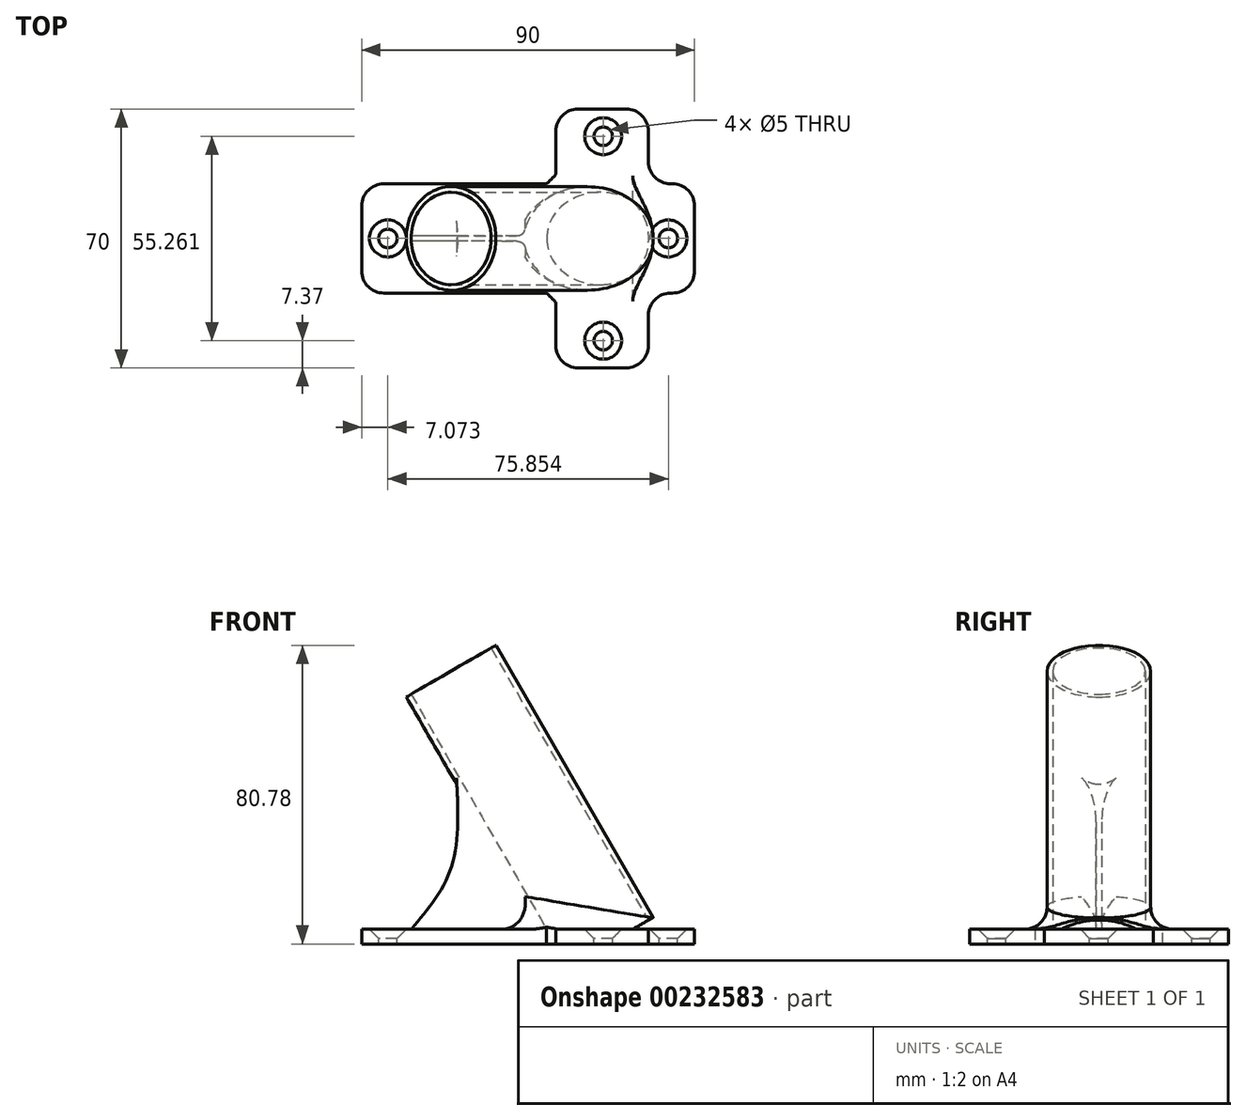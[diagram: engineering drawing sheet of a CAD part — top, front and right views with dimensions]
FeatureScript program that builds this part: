
annotation { "Feature Type Name" : "Feature", "Feature Type Description" : "" }
export const myFeature = defineFeature(function(context is Context, id is Id, definition is map)
    precondition{}
    {
        {
            var Q0;
            Q0=qCreatedBy(makeId("Top.planeOp"),FACE);
            var sketch = newSketch(context, id + "F0", { "sketchPlane" : qUnion([Q0])});
            skLineSegment(sketch, "E0.bottom", {"start": v(45, 14.77) * mm, "end": v(32.5, 14.77) * mm});
            skLineSegment(sketch, "E0.top", {"start": v(45, -14.77) * mm, "end": v(32.5, -14.77) * mm});
            skLineSegment(sketch, "E0.left", {"start": v(45, 14.77) * mm, "end": v(45, -14.77) * mm});
            skLineSegment(sketch, "E0.right", {"start": v(-45, 14.77) * mm, "end": v(-45, -14.77) * mm});
            skPoint(sketch, "E0.middle", {"position": v(0, 0) * mm});
            skCircle(sketch, "E1", {"center": v(37.93, 0) * mm, "radius": 2.5 * mm});
            skCircle(sketch, "E2.MirrorC", {"center": v(-37.93, 0) * mm, "radius": 2.5 * mm});
            skLineSegment(sketch, "E3", {"start": v(-37.93, 0) * mm, "end": v(37.93, 0) * mm, "construction": true});
            skLineSegment(sketch, "E4.bottom", {"start": v(32.5, 35) * mm, "end": v(7.5, 35) * mm});
            skLineSegment(sketch, "E4.top", {"start": v(32.5, -35) * mm, "end": v(7.5, -35) * mm});
            skLineSegment(sketch, "E4.left", {"start": v(32.5, 35) * mm, "end": v(32.5, 14.77) * mm});
            skLineSegment(sketch, "E4.right", {"start": v(7.5, 35) * mm, "end": v(7.5, 14.77) * mm});
            skPoint(sketch, "E4.middle", {"position": v(20, 0) * mm});
            skLineSegment(sketch, "E5.trimOffspring", {"start": v(7.5, -14.77) * mm, "end": v(-45, -14.77) * mm});
            skLineSegment(sketch, "E6.trimOffspring", {"start": v(7.5, 14.77) * mm, "end": v(-45, 14.77) * mm});
            skLineSegment(sketch, "E7.trimOffspring", {"start": v(7.5, -14.77) * mm, "end": v(7.5, -35) * mm});
            skLineSegment(sketch, "E8.trimOffspring", {"start": v(32.5, -14.77) * mm, "end": v(32.5, -35) * mm});
            skCircle(sketch, "E9", {"center": v(20.3, -27.63) * mm, "radius": 2.5 * mm});
            skCircle(sketch, "E10.MirrorC", {"center": v(20.3, 27.63) * mm, "radius": 2.5 * mm});
            skSolve(sketch);
        }
        {
            var Q0;
            Q0=qCreatedBy(makeId("Front.planeOp"),FACE);
            var sketch = newSketch(context, id + "F1", { "sketchPlane" : qUnion([Q0])});
            skLineSegment(sketch, "E11", {"start": v(19.46, 0) * mm, "end": v(14.34, 8.88) * mm, "construction": true});
            skLineSegment(sketch, "E12", {"start": v(-10, 76.03) * mm, "end": v(30, 6.75) * mm});
            skLineSegment(sketch, "E13", {"start": v(30, 6.75) * mm, "end": v(31.3, 7.5) * mm});
            skLineSegment(sketch, "E14", {"start": v(31.3, 7.5) * mm, "end": v(-8.7, 76.78) * mm});
            skLineSegment(sketch, "E15", {"start": v(-8.7, 76.78) * mm, "end": v(-10, 76.03) * mm});
            skSolve(sketch);
        }
        {
            var Q0;
            Q0=makeQuery(id+"F1.imprint","IMPRINT",FACE,{"disambiguationData":[TD([[makeQuery(id+"F1.imprint","IMPRINT",EDGE,{"derivedFrom":sQuery(id+"F1.wireOp",EDGE,"E12")}),1.0]])]});
            var Q1;
            Q1=sQuery(id+"F1.wireOp",EDGE,"E11");
            revolve(context, id + "F2", {"entities" : qUnion([Q0]), "axis" : qUnion([Q1]), "revolveType" : RevolveType.FULL});
        }
        {
            var Q0;
            Q0=makeQuery(id+"F0.imprint","IMPRINT",FACE,{"disambiguationData":[TD([[makeQuery(id+"F0.imprint","IMPRINT",EDGE,{"derivedFrom":sQuery(id+"F0.wireOp",EDGE,"k1UX8Zoy-U4vW-ooh1-YawX-v9qnedj7sq2Y.bottom")}),1.0]])]});
            var Q1;
            Q1=makeQuery(id+"F0.imprint","IMPRINT",FACE,{"disambiguationData":[TD([[makeQuery(id+"F0.imprint","IMPRINT",EDGE,{"derivedFrom":sQuery(id+"F0.wireOp",EDGE,"E0.bottom")}),1.0]])]});
            extrude(context, id + "F3", {"entities" : qUnion([Q0, Q1]), "operationType" : NewBodyOperationType.ADD, "oppositeDirection" : true, "depth" : 4 * mm});
        }
        {
            var Q0;
            Q0=qCreatedBy(makeId("Front.planeOp"),FACE);
            var sketch = newSketch(context, id + "F4", { "sketchPlane" : qUnion([Q0])});
            skLineSegment(sketch, "E16", {"start": v(-19.4, 40.97) * mm, "end": v(4.39, 0) * mm});
            skLineSegment(sketch, "E17", {"start": v(4.39, 0) * mm, "end": v(-31.5, 0) * mm});
            skFitSpline(sketch, "E18", {"points": [v(-19.4, 40.97) * mm, v(-21.2, 15.47) * mm, v(-31.5, 0) * mm], "startDerivative": vector(3.61, -51.52) * mm, "endDerivative": vector(-23.7, -30.7) * mm});
            skSolve(sketch);
        }
        {
            var Q0;
            Q0=makeQuery(id+"F4.imprint","IMPRINT",FACE,{"disambiguationData":[TD([[makeQuery(id+"F4.imprint","IMPRINT",EDGE,{"derivedFrom":sQuery(id+"F4.wireOp",EDGE,"E16")}),-1.0]])]});
            extrude(context, id + "F5", {"entities" : qUnion([Q0]), "operationType" : NewBodyOperationType.ADD, "endBound" : BoundingType.SYMMETRIC, "depth" : 1.5 * mm});
        }
        {
            var Q0;
            Q0=makeQuery(id+"F2.opRevolve","SWEPT_FACE",FACE,{"disambiguationData":[OSD([sQuery(id+"F1.wireOp",EDGE,"E13")])]});
            extrude(context, id + "F6", {"entities" : qUnion([Q0]), "operationType" : NewBodyOperationType.ADD, "depth" : 5 * mm});
        }
        {
            var Q0;
            Q0=makeQuery(id+"F6.boolean.opBoolean","INTERSECT",EDGE,{"disambiguationData":[OD(1.0)],"derivedFrom":[makeQuery(id+"F3.opExtrude","CAP_FACE",FACE,{"disambiguationData":[OSD([sQuery(id+"F0.wireOp",EDGE,"E0.bottom"),sQuery(id+"F0.wireOp",EDGE,"E0.top"),sQuery(id+"F0.wireOp",EDGE,"E0.left"),sQuery(id+"F0.wireOp",EDGE,"E0.right"),sQuery(id+"F0.wireOp",EDGE,"E1"),sQuery(id+"F0.wireOp",EDGE,"E2.MirrorC")])],"isStart":true}),makeQuery(id+"F6.opExtrude","SWEPT_FACE",FACE,{"disambiguationData":[OSD([sQuery(id+"F1.wireOp",EDGE,"E13"),sQuery(id+"F1.wireOp",EDGE,"E14")])]})]});
            var Q1;
            Q1=makeQuery(id+"F5.opExtrude","CAP_EDGE",EDGE,{"disambiguationData":[OSD([sQuery(id+"F4.wireOp",EDGE,"E17")])],"isStart":true});
            var Q2;
            Q2=makeQuery(id+"F6.boolean.opBoolean","INTERSECT",EDGE,{"disambiguationData":[OD(0.0)],"derivedFrom":[makeQuery(id+"F3.opExtrude","CAP_FACE",FACE,{"disambiguationData":[OSD([sQuery(id+"F0.wireOp",EDGE,"E0.bottom"),sQuery(id+"F0.wireOp",EDGE,"E0.top"),sQuery(id+"F0.wireOp",EDGE,"E0.left"),sQuery(id+"F0.wireOp",EDGE,"E0.right"),sQuery(id+"F0.wireOp",EDGE,"E1"),sQuery(id+"F0.wireOp",EDGE,"E2.MirrorC")])],"isStart":true}),makeQuery(id+"F6.opExtrude","SWEPT_FACE",FACE,{"disambiguationData":[OSD([sQuery(id+"F1.wireOp",EDGE,"E13"),sQuery(id+"F1.wireOp",EDGE,"E14")])]})]});
            var Q3;
            Q3=makeQuery(id+"F5.opExtrude","CAP_EDGE",EDGE,{"disambiguationData":[OSD([sQuery(id+"F4.wireOp",EDGE,"E17")])],"isStart":false});
            var Q4;
            Q4=makeQuery(id+"F3.opExtrude","SWEPT_EDGE",EDGE,{"disambiguationData":[OSD([sQuery(id+"F0.wireOp",EDGE,"E0.top"),sQuery(id+"F0.wireOp",EDGE,"E0.right")])]});
            var Q5;
            Q5=makeQuery(id+"F3.opExtrude","SWEPT_EDGE",EDGE,{"disambiguationData":[OSD([sQuery(id+"F0.wireOp",EDGE,"E0.bottom"),sQuery(id+"F0.wireOp",EDGE,"E0.right")])]});
            var Q6;
            Q6=makeQuery(id+"F3.opExtrude","SWEPT_EDGE",EDGE,{"disambiguationData":[OSD([sQuery(id+"F0.wireOp",EDGE,"E0.bottom"),sQuery(id+"F0.wireOp",EDGE,"E0.left")])]});
            var Q7;
            Q7=makeQuery(id+"F3.opExtrude","SWEPT_EDGE",EDGE,{"disambiguationData":[OSD([sQuery(id+"F0.wireOp",EDGE,"E0.top"),sQuery(id+"F0.wireOp",EDGE,"E0.left")])]});
            var Q8;
            Q8=makeQuery(id+"F5.boolean.opBoolean","INTERSECT",EDGE,{"derivedFrom":[makeQuery(id+"F2.opRevolve","SWEPT_FACE",FACE,{"disambiguationData":[OSD([sQuery(id+"F1.wireOp",EDGE,"E14")])]}),makeQuery(id+"F5.opExtrude","CAP_FACE",FACE,{"disambiguationData":[OSD([sQuery(id+"F4.wireOp",EDGE,"E16"),sQuery(id+"F4.wireOp",EDGE,"E17"),sQuery(id+"F4.wireOp",EDGE,"GgjzEMgf-FbxD-iaOB-yrJi-r67IALF0cPDc")])],"isStart":false})]});
            var Q9;
            Q9=makeQuery(id+"F5.boolean.opBoolean","INTERSECT",EDGE,{"derivedFrom":[makeQuery(id+"F2.opRevolve","SWEPT_FACE",FACE,{"disambiguationData":[OSD([sQuery(id+"F1.wireOp",EDGE,"E14")])]}),makeQuery(id+"F5.opExtrude","CAP_FACE",FACE,{"disambiguationData":[OSD([sQuery(id+"F4.wireOp",EDGE,"E16"),sQuery(id+"F4.wireOp",EDGE,"E17"),sQuery(id+"F4.wireOp",EDGE,"GgjzEMgf-FbxD-iaOB-yrJi-r67IALF0cPDc")])],"isStart":true})]});
            var Q10;
            Q10=makeQuery(id+"F3.opExtrude","SWEPT_EDGE",EDGE,{"disambiguationData":[OSD([sQuery(id+"F0.wireOp",EDGE,"E4.top"),sQuery(id+"F0.wireOp",EDGE,"E7.trimOffspring")])]});
            var Q11;
            Q11=makeQuery(id+"F3.opExtrude","SWEPT_EDGE",EDGE,{"disambiguationData":[OSD([sQuery(id+"F0.wireOp",EDGE,"E4.top"),sQuery(id+"F0.wireOp",EDGE,"E8.trimOffspring")])]});
            var Q12;
            Q12=makeQuery(id+"F3.opExtrude","SWEPT_EDGE",EDGE,{"disambiguationData":[OSD([sQuery(id+"F0.wireOp",EDGE,"E4.bottom"),sQuery(id+"F0.wireOp",EDGE,"E4.left")])]});
            var Q13;
            Q13=makeQuery(id+"F3.opExtrude","SWEPT_EDGE",EDGE,{"disambiguationData":[OSD([sQuery(id+"F0.wireOp",EDGE,"E4.bottom"),sQuery(id+"F0.wireOp",EDGE,"E4.right")])]});
            fillet(context, id + "F7", {"entities" : qUnion([Q0, Q1, Q2, Q3, Q4, Q5, Q6, Q7, Q8, Q9, Q10, Q11, Q12, Q13]), "radius" : 6 * mm, "tangentPropagation" : true, "allowEdgeOverflow" : false});
        }
        {
            var Q0;
            Q0=makeQuery(id+"F3.opExtrude","CAP_EDGE",EDGE,{"disambiguationData":[OSD([sQuery(id+"F0.wireOp",EDGE,"E2.MirrorC")])],"isStart":true});
            var Q1;
            Q1=makeQuery(id+"F3.opExtrude","CAP_EDGE",EDGE,{"disambiguationData":[OSD([sQuery(id+"F0.wireOp",EDGE,"E1")])],"isStart":true});
            var Q2;
            Q2=makeQuery(id+"F3.opExtrude","CAP_EDGE",EDGE,{"disambiguationData":[OSD([sQuery(id+"F0.wireOp",EDGE,"E9")])],"isStart":true});
            var Q3;
            Q3=makeQuery(id+"F3.opExtrude","CAP_EDGE",EDGE,{"disambiguationData":[OSD([sQuery(id+"F0.wireOp",EDGE,"E10.MirrorC")])],"isStart":true});
            var Q4;
            Q4=makeQuery(id+"F3.opExtrude","SWEPT_EDGE",EDGE,{"disambiguationData":[OSD([sQuery(id+"F0.wireOp",EDGE,"E5.trimOffspring"),sQuery(id+"F0.wireOp",EDGE,"E7.trimOffspring")])]});
            var Q5;
            Q5=makeQuery(id+"F3.opExtrude","SWEPT_EDGE",EDGE,{"disambiguationData":[OSD([sQuery(id+"F0.wireOp",EDGE,"E4.right"),sQuery(id+"F0.wireOp",EDGE,"E6.trimOffspring")])]});
            chamfer(context, id + "F8", {"entities" : qUnion([Q0, Q1, Q2, Q3, Q4, Q5]), "width" : 2.5 * mm, "tangentPropagation" : true});
        }
        {
            var Q0;
            Q0=qCreatedBy(makeId("Top.planeOp"),FACE);
            cPlane(context, id + "F9", {"entities" : qUnion([Q0]), "cplaneType" : CPlaneType.OFFSET, "offset" : 4 * mm, "oppositeDirection" : true, "width" : 150 * mm, "height" : 150 * mm});
        }
        {
            var Q0;
            Q0=qCreatedBy(id+"F9.planeOp",FACE);
            var sketch = newSketch(context, id + "F10", { "sketchPlane" : qUnion([Q0])});
            skCircle(sketch, "E19", {"center": v(0, 0) * mm, "radius": 29.9 * mm});
            skSolve(sketch);
        }
        {
            var Q0;
            Q0=makeQuery(id+"F10.imprint","IMPRINT",FACE,{"disambiguationData":[TD([[makeQuery(id+"F10.imprint","IMPRINT",EDGE,{"derivedFrom":sQuery(id+"F10.wireOp",EDGE,"E19")}),1.0]])]});
            extrude(context, id + "F11", {"entities" : qUnion([Q0]), "operationType" : NewBodyOperationType.REMOVE, "oppositeDirection" : true, "depth" : 25 * mm});
        }
    });
